# Revit family: Drinking_Fountain-Haws_Corporation-Bottle_Filler_1920
name_source: partatom
category: Plumbing Fixtures
revit_build: Autodesk Revit Architecture 2015 (Build: 20140606_1530(x64)
units: mm (PartAtom-declared; Revit-internal decimal feet)

## types (3) — shared parameters
Bracket = Metal - Haws Corporation - Satin Stainless Steel
Default Elevation = 4' - 0"
Description = Bottle filler can be a stand-alone station, or mounted above Haws 1001, 1011, 1107L and 1117L series drinking fountain models.
HW Connection = No
Manufacturer = Haws Corporation
Model = 1920
Plate Finish = Metal - Haws Corporation - Satin Stainless Steel
Product Documentation Link = https://www.hawsco.com
Product Name = Bottle Filler
Product Page URL = https://www.hawsco.com
SKU = 10-101
URL = https://www.hawsco.com
Vent Connection = No
Version = 2014-v1.0a
Waste Connection = No

## per-type parameters (varying)
| type | BP15 Panel | BP32 Panel | Plate Model |
| 1920 | No | No | No Panel Option Selected |
| 1920 with BP15 Panel | Yes | No | BP15 |
| 1920 with BP32 Panel | No | Yes | BP32 |

## geometry (parser evidence)
native form markers: Blend x20, Sweep x2
no freeform markers — native parametric forms only
